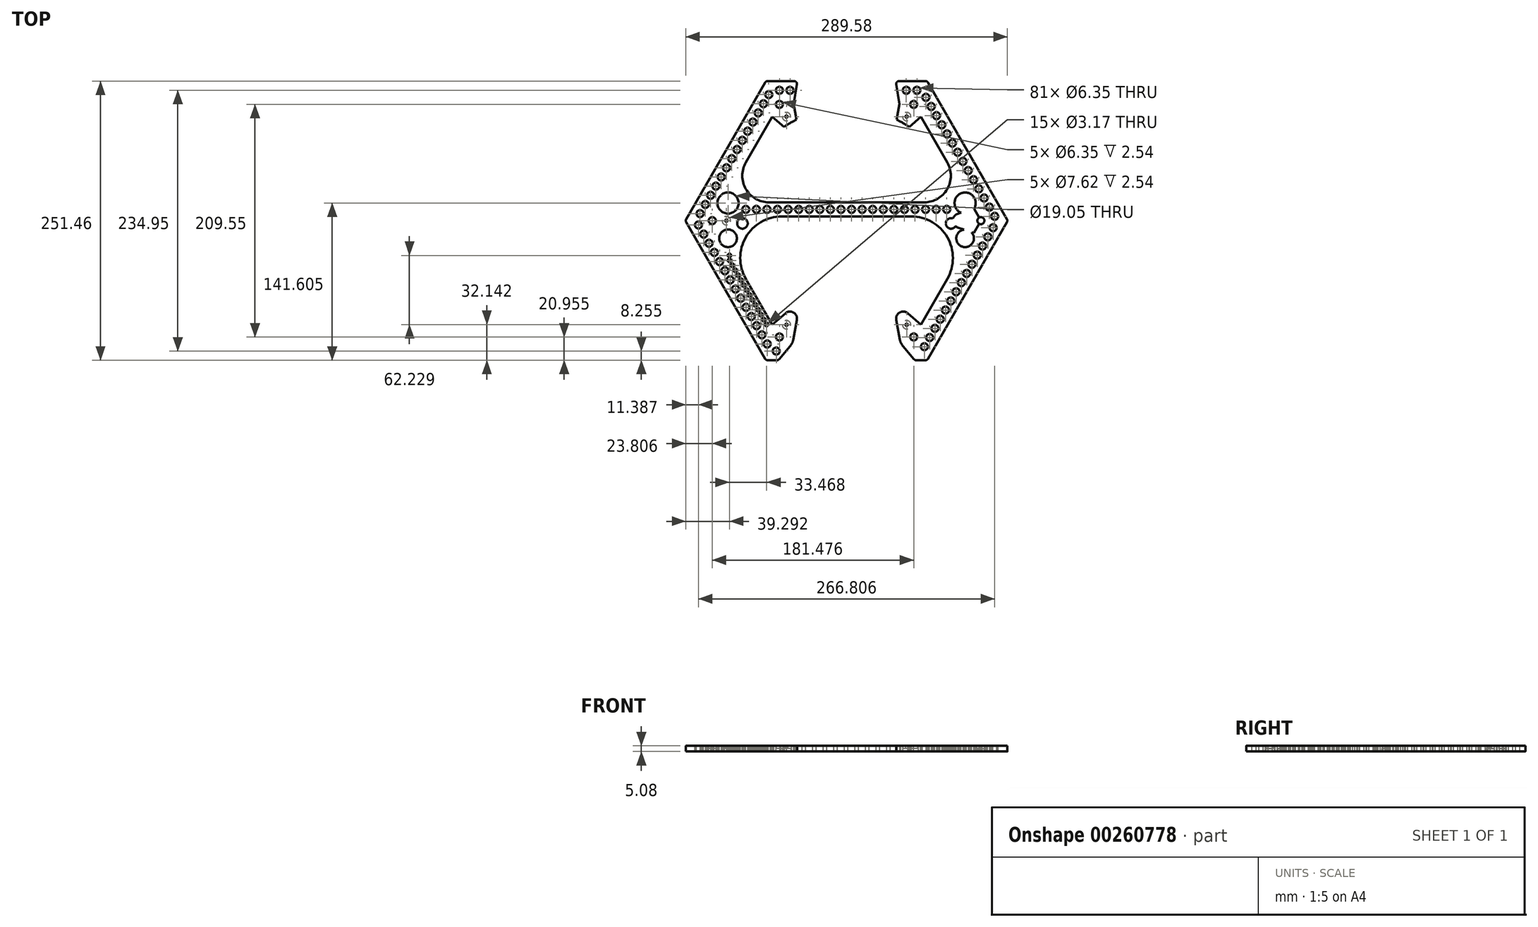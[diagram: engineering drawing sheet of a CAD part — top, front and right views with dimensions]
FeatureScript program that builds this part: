
annotation { "Feature Type Name" : "Feature", "Feature Type Description" : "" }
export const myFeature = defineFeature(function(context is Context, id is Id, definition is map)
    precondition{}
    {
        {
            var Q0;
            Q0=qCreatedBy(makeId("Top.planeOp"),FACE);
            var sketch = newSketch(context, id + "F0", { "sketchPlane" : qUnion([Q0])});
            skCircle(sketch, "E0.cCircle", {"center": v(0, 0) * mm, "radius": 125.73 * mm, "construction": true});
            skLineSegment(sketch, "E0.0", {"start": v(-72.6, 125.73) * mm, "end": v(72.6, 125.73) * mm, "construction": true});
            skLineSegment(sketch, "E0.1", {"start": v(72.6, 125.73) * mm, "end": v(145.18, 0) * mm, "construction": true});
            skLineSegment(sketch, "E0.2", {"start": v(145.18, 0) * mm, "end": v(72.6, -125.73) * mm, "construction": true});
            skLineSegment(sketch, "E0.3", {"start": v(72.6, -125.73) * mm, "end": v(-72.6, -125.73) * mm, "construction": true});
            skLineSegment(sketch, "E0.4", {"start": v(-72.6, -125.73) * mm, "end": v(-145.18, 0) * mm, "construction": true});
            skLineSegment(sketch, "E0.5", {"start": v(-145.18, 0) * mm, "end": v(-72.6, 125.73) * mm, "construction": true});
            skPoint(sketch, "E0.0.midPoint", {"position": v(0, 125.73) * mm});
            skLineSegment(sketch, "E1.bottom", {"start": v(-23.4, 2.97) * mm, "end": v(23.4, 2.97) * mm, "construction": true});
            skLineSegment(sketch, "E1.top", {"start": v(-23.4, -102.03) * mm, "end": v(23.4, -102.03) * mm, "construction": true});
            skLineSegment(sketch, "E1.left", {"start": v(-61.5, -35.13) * mm, "end": v(-61.5, -63.93) * mm, "construction": true});
            skLineSegment(sketch, "E1.right", {"start": v(61.5, -35.13) * mm, "end": v(61.5, -63.93) * mm, "construction": true});
            skPoint(sketch, "E2", {"position": v(0, -49.53) * mm});
            skPoint(sketch, "E2.positionSnap0", {"position": v(61.5, -49.53) * mm});
            skPoint(sketch, "E2.positionSnap1", {"position": v(0, 2.97) * mm});
            skPoint(sketch, "E3.visualSharp", {"position": v(-61.5, 2.97) * mm});
            skArc(sketch, "E3.filletArc", {"start": v(-23.4, 2.97) * mm, "mid": v(-50.34, -8.19) * mm, "end": v(-61.5, -35.13) * mm, "construction": true});
            skPoint(sketch, "E4.visualSharp", {"position": v(-61.5, -102.03) * mm});
            skArc(sketch, "E4.filletArc", {"start": v(-61.5, -63.93) * mm, "mid": v(-50.34, -90.87) * mm, "end": v(-23.4, -102.03) * mm, "construction": true});
            skPoint(sketch, "E5.visualSharp", {"position": v(61.5, -102.03) * mm});
            skArc(sketch, "E5.filletArc", {"start": v(23.4, -102.03) * mm, "mid": v(50.34, -90.87) * mm, "end": v(61.5, -63.93) * mm, "construction": true});
            skPoint(sketch, "E6.visualSharp", {"position": v(61.5, 2.97) * mm});
            skArc(sketch, "E6.filletArc", {"start": v(61.5, -35.13) * mm, "mid": v(50.34, -8.19) * mm, "end": v(23.4, 2.97) * mm, "construction": true});
            skLineSegment(sketch, "E7.bottom", {"start": v(-44.25, 106.48) * mm, "end": v(44.25, 106.48) * mm, "construction": true});
            skLineSegment(sketch, "E7.top", {"start": v(-44.25, 17.98) * mm, "end": v(44.25, 17.98) * mm, "construction": true});
            skLineSegment(sketch, "E7.left", {"start": v(-44.25, 106.48) * mm, "end": v(-44.25, 17.98) * mm, "construction": true});
            skLineSegment(sketch, "E7.right", {"start": v(44.25, 106.48) * mm, "end": v(44.25, 17.98) * mm, "construction": true});
            skPoint(sketch, "E8", {"position": v(0, 106.48) * mm});
            skPoint(sketch, "E9", {"position": v(0, 62.23) * mm});
            skPoint(sketch, "E9.positionSnap0", {"position": v(-44.25, 62.23) * mm});
            skSolve(sketch);
        }
        {
            var Q0;
            Q0=qCreatedBy(makeId("Top.planeOp"),FACE);
            var sketch = newSketch(context, id + "F1", { "sketchPlane" : qUnion([Q0])});
            skLineSegment(sketch, "E10", {"start": v(-73.32, 124.46) * mm, "end": v(-144.45, 1.27) * mm});
            skLineSegment(sketch, "E11", {"start": v(-144.45, -1.27) * mm, "end": v(-73.32, -124.46) * mm});
            skLineSegment(sketch, "E12", {"start": v(-71.12, -125.73) * mm, "end": v(-62.68, -125.73) * mm});
            skLineSegment(sketch, "E13", {"start": v(-71.12, 125.73) * mm, "end": v(-47.23, 125.73) * mm});
            skLineSegment(sketch, "E14", {"start": v(47.23, 125.73) * mm, "end": v(71.12, 125.73) * mm});
            skLineSegment(sketch, "E15", {"start": v(73.32, 124.46) * mm, "end": v(144.45, 1.27) * mm});
            skLineSegment(sketch, "E16", {"start": v(144.45, -1.27) * mm, "end": v(73.32, -124.46) * mm});
            skLineSegment(sketch, "E17", {"start": v(71.12, -125.73) * mm, "end": v(62.68, -125.73) * mm});
            skCircle(sketch, "E18.cCircle", {"center": v(0, 0) * mm, "radius": 104.78 * mm, "construction": true});
            skLineSegment(sketch, "E18.0", {"start": v(-60.5, 104.78) * mm, "end": v(60.5, 104.78) * mm, "construction": true});
            skLineSegment(sketch, "E18.1", {"start": v(60.5, 104.78) * mm, "end": v(120.98, 0) * mm});
            skLineSegment(sketch, "E18.2", {"start": v(120.98, 0) * mm, "end": v(60.5, -104.78) * mm});
            skLineSegment(sketch, "E18.3", {"start": v(60.5, -104.77) * mm, "end": v(-60.5, -104.78) * mm, "construction": true});
            skLineSegment(sketch, "E18.4", {"start": v(-60.5, -104.78) * mm, "end": v(-120.98, 0) * mm});
            skLineSegment(sketch, "E18.5", {"start": v(-120.98, 0) * mm, "end": v(-60.5, 104.78) * mm});
            skPoint(sketch, "E18.0.midPoint", {"position": v(0, 104.78) * mm});
            skCircle(sketch, "E19", {"center": v(-60.5, 104.78) * mm, "radius": 3.18 * mm});
            skCircle(sketch, "E20", {"center": v(60.5, 104.78) * mm, "radius": 3.18 * mm});
            skCircle(sketch, "E21", {"center": v(-120.98, 0) * mm, "radius": 3.18 * mm});
            skCircle(sketch, "E22", {"center": v(120.98, 0) * mm, "radius": 3.17 * mm});
            skCircle(sketch, "E23", {"center": v(60.5, -104.78) * mm, "radius": 3.18 * mm});
            skCircle(sketch, "E24", {"center": v(-60.5, -104.78) * mm, "radius": 3.17 * mm});
            skCircle(sketch, "E25", {"center": v(-60.5, -104.78) * mm, "radius": 12.7 * mm, "construction": true});
            skCircle(sketch, "E26", {"center": v(60.5, -104.78) * mm, "radius": 12.7 * mm, "construction": true});
            skLineSegment(sketch, "E27", {"start": v(-60.74, -124.82) * mm, "end": v(-50.76, -112.94) * mm});
            skPoint(sketch, "E28.visualSharp", {"position": v(-72.6, -125.73) * mm});
            skArc(sketch, "E28.filletArc", {"start": v(-73.32, -124.46) * mm, "mid": v(-72.4, -125.39) * mm, "end": v(-71.12, -125.73) * mm});
            skPoint(sketch, "E29.visualSharp", {"position": v(-61.5, -125.73) * mm});
            skArc(sketch, "E29.filletArc", {"start": v(-62.68, -125.73) * mm, "mid": v(-61.61, -125.5) * mm, "end": v(-60.74, -124.82) * mm});
            skCircle(sketch, "E30", {"center": v(-120.98, 0) * mm, "radius": 12.7 * mm, "construction": true});
            skCircle(sketch, "E31", {"center": v(120.98, 0) * mm, "radius": 12.7 * mm, "construction": true});
            skCircle(sketch, "E32", {"center": v(60.5, 104.78) * mm, "radius": 12.7 * mm, "construction": true});
            skCircle(sketch, "E33", {"center": v(-60.5, 104.78) * mm, "radius": 12.7 * mm, "construction": true});
            skLineSegment(sketch, "E34", {"start": v(-44.72, 122.79) * mm, "end": v(-47.95, 102.75) * mm});
            skLineSegment(sketch, "E35", {"start": v(-51.48, 95.8) * mm, "end": v(-51.07, 96.26) * mm});
            skArc(sketch, "E36", {"start": v(-51.07, 96.26) * mm, "mid": v(-49.04, 99.28) * mm, "end": v(-47.95, 102.75) * mm});
            skArc(sketch, "E37", {"start": v(-50.76, -112.94) * mm, "mid": v(-47.8, -104.54) * mm, "end": v(-51.07, -96.26) * mm});
            skLineSegment(sketch, "E38", {"start": v(60.74, -124.82) * mm, "end": v(50.76, -112.94) * mm});
            skLineSegment(sketch, "E39", {"start": v(44.72, 122.79) * mm, "end": v(47.95, 102.75) * mm});
            skLineSegment(sketch, "E40", {"start": v(51.48, 95.8) * mm, "end": v(51.07, 96.26) * mm});
            skArc(sketch, "E41", {"start": v(47.95, 102.75) * mm, "mid": v(49.04, 99.28) * mm, "end": v(51.07, 96.26) * mm});
            skArc(sketch, "E42", {"start": v(51.07, -96.26) * mm, "mid": v(47.8, -104.54) * mm, "end": v(50.76, -112.94) * mm});
            skPoint(sketch, "E43.visualSharp", {"position": v(-90.74, -52.39) * mm});
            skPoint(sketch, "E44.visualSharp", {"position": v(90.74, -52.39) * mm});
            skPoint(sketch, "E45.visualSharp", {"position": v(-90.74, 52.39) * mm});
            skPoint(sketch, "E46.visualSharp", {"position": v(90.74, 52.39) * mm});
            skPoint(sketch, "E47.visualSharp", {"position": v(-44.25, 125.73) * mm});
            skArc(sketch, "E47.filletArc", {"start": v(-44.72, 122.79) * mm, "mid": v(-45.3, 124.84) * mm, "end": v(-47.23, 125.73) * mm});
            skPoint(sketch, "E48.visualSharp", {"position": v(-145.18, 0) * mm});
            skArc(sketch, "E48.filletArc", {"start": v(-144.45, 1.27) * mm, "mid": v(-144.79, 0) * mm, "end": v(-144.45, -1.27) * mm});
            skPoint(sketch, "E49.visualSharp", {"position": v(-72.6, 125.73) * mm});
            skArc(sketch, "E49.filletArc", {"start": v(-71.12, 125.73) * mm, "mid": v(-72.4, 125.39) * mm, "end": v(-73.32, 124.46) * mm});
            skPoint(sketch, "E50.visualSharp", {"position": v(44.25, 125.73) * mm});
            skArc(sketch, "E50.filletArc", {"start": v(47.23, 125.73) * mm, "mid": v(45.3, 124.84) * mm, "end": v(44.72, 122.79) * mm});
            skPoint(sketch, "E51.visualSharp", {"position": v(72.6, 125.73) * mm});
            skArc(sketch, "E51.filletArc", {"start": v(73.32, 124.46) * mm, "mid": v(72.4, 125.39) * mm, "end": v(71.12, 125.73) * mm});
            skPoint(sketch, "E52.visualSharp", {"position": v(145.18, 0) * mm});
            skArc(sketch, "E52.filletArc", {"start": v(144.45, -1.27) * mm, "mid": v(144.79, 0) * mm, "end": v(144.45, 1.27) * mm});
            skPoint(sketch, "E53.visualSharp", {"position": v(72.6, -125.73) * mm});
            skArc(sketch, "E53.filletArc", {"start": v(71.12, -125.73) * mm, "mid": v(72.4, -125.39) * mm, "end": v(73.32, -124.46) * mm});
            skPoint(sketch, "E54.visualSharp", {"position": v(61.5, -125.73) * mm});
            skArc(sketch, "E54.filletArc", {"start": v(60.74, -124.82) * mm, "mid": v(61.61, -125.5) * mm, "end": v(62.68, -125.73) * mm});
            skLineSegment(sketch, "E55", {"start": v(-48, 107.1) * mm, "end": v(-44.72, 89.44) * mm});
            skLineSegment(sketch, "E56", {"start": v(-55.1, 83.45) * mm, "end": v(-68.74, 95.12) * mm});
            skLineSegment(sketch, "E57", {"start": v(-41.44, 71.78) * mm, "end": v(-60.5, 104.78) * mm, "construction": true});
            skArc(sketch, "E58.filletArc", {"start": v(-55.1, 83.45) * mm, "mid": v(-47.8, 82.78) * mm, "end": v(-44.72, 89.44) * mm});
            skPoint(sketch, "E59.startSnap0", {"position": v(46.34, 112.77) * mm});
            skLineSegment(sketch, "E60", {"start": v(48, 107.1) * mm, "end": v(44.72, 89.44) * mm});
            skLineSegment(sketch, "E61", {"start": v(55.1, 83.45) * mm, "end": v(68.74, 95.12) * mm});
            skLineSegment(sketch, "E62", {"start": v(41.44, 71.78) * mm, "end": v(60.5, 104.78) * mm, "construction": true});
            skArc(sketch, "E63.filletArc", {"start": v(44.72, 89.44) * mm, "mid": v(47.8, 82.78) * mm, "end": v(55.1, 83.45) * mm});
            skLineSegment(sketch, "E64.MirrorCS", {"start": v(-41.44, -71.78) * mm, "end": v(-60.5, -104.78) * mm, "construction": true});
            skLineSegment(sketch, "E65.MirrorCS", {"start": v(41.44, -71.78) * mm, "end": v(60.5, -104.78) * mm, "construction": true});
            skLineSegment(sketch, "E66.MirrorCS", {"start": v(55.1, -83.45) * mm, "end": v(68.74, -95.12) * mm});
            skArc(sketch, "E67.MirrorCS", {"start": v(44.72, -89.44) * mm, "mid": v(47.8, -82.78) * mm, "end": v(55.1, -83.45) * mm});
            skLineSegment(sketch, "E68.MirrorCS", {"start": v(48, -107.1) * mm, "end": v(44.72, -89.44) * mm});
            skArc(sketch, "E69.MirrorCS", {"start": v(-55.1, -83.45) * mm, "mid": v(-47.8, -82.78) * mm, "end": v(-44.72, -89.44) * mm});
            skLineSegment(sketch, "E70.MirrorCS", {"start": v(-48, -107.1) * mm, "end": v(-44.72, -89.44) * mm});
            skLineSegment(sketch, "E71.MirrorCS", {"start": v(-55.1, -83.45) * mm, "end": v(-68.74, -95.12) * mm});
            skLineSegment(sketch, "E72", {"start": v(-116.75, 11.97) * mm, "end": v(-99.82, 5.99) * mm});
            skLineSegment(sketch, "E73", {"start": v(-99.82, -5.99) * mm, "end": v(-116.75, -11.97) * mm});
            skLineSegment(sketch, "E74", {"start": v(-82.88, 0) * mm, "end": v(-120.98, 0) * mm, "construction": true});
            skPoint(sketch, "E75.visualSharp", {"position": v(-82.88, 0) * mm});
            skArc(sketch, "E75.filletArc", {"start": v(-99.82, -5.99) * mm, "mid": v(-95.58, 0) * mm, "end": v(-99.82, 5.99) * mm});
            skLineSegment(sketch, "E76.MirrorCS", {"start": v(116.75, 11.97) * mm, "end": v(99.82, 5.99) * mm});
            skArc(sketch, "E77.MirrorCS", {"start": v(99.82, -5.99) * mm, "mid": v(95.58, 0) * mm, "end": v(99.82, 5.99) * mm});
            skLineSegment(sketch, "E78.MirrorCS", {"start": v(82.88, 0) * mm, "end": v(120.98, 0) * mm, "construction": true});
            skLineSegment(sketch, "E79.MirrorCS", {"start": v(99.82, -5.99) * mm, "end": v(116.75, -11.97) * mm});
            skCircle(sketch, "E80", {"center": v(-108.28, 0) * mm, "radius": 1.08 * mm});
            skCircle(sketch, "E81", {"center": v(-54.14, -93.78) * mm, "radius": 1.08 * mm});
            skCircle(sketch, "E82", {"center": v(54.14, -93.78) * mm, "radius": 1.08 * mm});
            skCircle(sketch, "E83", {"center": v(108.28, 0) * mm, "radius": 1.08 * mm});
            skCircle(sketch, "E84", {"center": v(54.14, 93.78) * mm, "radius": 1.08 * mm});
            skCircle(sketch, "E85", {"center": v(-54.14, 93.78) * mm, "radius": 1.08 * mm});
            skArc(sketch, "E86", {"start": v(-58.26, 3.86) * mm, "mid": v(-90.74, -14.9) * mm, "end": v(-90.74, -52.39) * mm});
            skArc(sketch, "E87", {"start": v(-90.74, 52.39) * mm, "mid": v(-90.74, 28.47) * mm, "end": v(-70.02, 16.5) * mm});
            skLineSegment(sketch, "E88", {"start": v(-70.02, 16.5) * mm, "end": v(70.02, 16.5) * mm});
            skLineSegment(sketch, "E89", {"start": v(-58.26, 3.86) * mm, "end": v(58.26, 3.86) * mm});
            skPoint(sketch, "E90", {"position": v(0, 3.86) * mm});
            skPoint(sketch, "E91", {"position": v(0, 16.5) * mm});
            skArc(sketch, "E92", {"start": v(90.74, -52.39) * mm, "mid": v(90.74, -14.9) * mm, "end": v(58.26, 3.86) * mm});
            skArc(sketch, "E93", {"start": v(70.02, 16.5) * mm, "mid": v(90.74, 28.47) * mm, "end": v(90.74, 52.39) * mm});
            skSolve(sketch);
        }
        {
            var Q0;
            {var subQ2=sQuery(id+"F1.wireOp",EDGE,"E35");Q0=makeQuery(id+"F1.imprint","IMPRINT",FACE,{"disambiguationData":[TD([[makeQuery(id+"F1.imprint","IMPRINT",EDGE,{"derivedFrom":subQ2}),-1.0]])]});}
            var Q1;
            {var subQ4=sQuery(id+"F1.wireOp",EDGE,"E69.MirrorCS");Q1=makeQuery(id+"F1.imprint","IMPRINT",FACE,{"disambiguationData":[TD([[makeQuery(id+"F1.imprint","IMPRINT",EDGE,{"derivedFrom":subQ4}),-1.0]])]});}
            var Q2;
            {var subQ6=sQuery(id+"F1.wireOp",EDGE,"E40");Q2=makeQuery(id+"F1.imprint","IMPRINT",FACE,{"disambiguationData":[TD([[makeQuery(id+"F1.imprint","IMPRINT",EDGE,{"derivedFrom":subQ6}),1.0]])]});}
            var Q3;
            {var subQ6=sQuery(id+"F1.wireOp",EDGE,"E67.MirrorCS");Q3=makeQuery(id+"F1.imprint","IMPRINT",FACE,{"disambiguationData":[TD([[makeQuery(id+"F1.imprint","IMPRINT",EDGE,{"derivedFrom":subQ6}),-1.0]])]});}
            var Q4;
            Q4=makeQuery(id+"F1.imprint","IMPRINT",FACE,{"disambiguationData":[TD([[makeQuery(id+"F1.imprint","IMPRINT",EDGE,{"derivedFrom":sQuery(id+"F1.wireOp",EDGE,"E10")}),1.0]])]});
            var Q5;
            Q5=makeQuery(id+"F1.imprint","IMPRINT",FACE,{"disambiguationData":[TD([[makeQuery(id+"F1.imprint","IMPRINT",EDGE,{"derivedFrom":sQuery(id+"F1.wireOp",EDGE,"E14")}),-1.0]])]});
            var Q6;
            {var subQ0=sQuery(id+"F1.wireOp",EDGE,"E75.filletArc");Q6=makeQuery(id+"F1.imprint","IMPRINT",FACE,{"disambiguationData":[TD([[makeQuery(id+"F1.imprint","IMPRINT",EDGE,{"derivedFrom":subQ0}),1.0]])]});}
            var Q7;
            {var subQ0=sQuery(id+"F1.wireOp",EDGE,"E77.MirrorCS");Q7=makeQuery(id+"F1.imprint","IMPRINT",FACE,{"disambiguationData":[TD([[makeQuery(id+"F1.imprint","IMPRINT",EDGE,{"derivedFrom":subQ0}),-1.0]])]});}
            var Q8;
            {var subQ11=sQuery(id+"F1.wireOp",EDGE,"E75.filletArc");Q8=makeQuery(id+"F1.imprint","IMPRINT",FACE,{"disambiguationData":[TD([[makeQuery(id+"F1.imprint","IMPRINT",EDGE,{"derivedFrom":subQ11}),-1.0]])]});}
            extrude(context, id + "F2", {"entities" : qUnion([Q0, Q1, Q2, Q3, Q4, Q5, Q6, Q7, Q8]), "depth" : 5.08 * mm});
        }
        {
            var Q0;
            Q0=makeQuery(id+"F1.imprint","IMPRINT",FACE,{"disambiguationData":[TD([[makeQuery(id+"F1.imprint","IMPRINT",EDGE,{"derivedFrom":sQuery(id+"F1.wireOp",EDGE,"E19")}),1.0]])]});
            var Q1;
            Q1=makeQuery(id+"F1.imprint","IMPRINT",FACE,{"disambiguationData":[TD([[makeQuery(id+"F1.imprint","IMPRINT",EDGE,{"derivedFrom":sQuery(id+"F1.wireOp",EDGE,"E20")}),1.0]])]});
            var Q2;
            Q2=makeQuery(id+"F1.imprint","IMPRINT",FACE,{"disambiguationData":[TD([[makeQuery(id+"F1.imprint","IMPRINT",EDGE,{"derivedFrom":sQuery(id+"F1.wireOp",EDGE,"E21")}),1.0]])]});
            var Q3;
            Q3=makeQuery(id+"F1.imprint","IMPRINT",FACE,{"disambiguationData":[TD([[makeQuery(id+"F1.imprint","IMPRINT",EDGE,{"derivedFrom":sQuery(id+"F1.wireOp",EDGE,"E22")}),1.0]])]});
            var Q4;
            Q4=makeQuery(id+"F1.imprint","IMPRINT",FACE,{"disambiguationData":[TD([[makeQuery(id+"F1.imprint","IMPRINT",EDGE,{"derivedFrom":sQuery(id+"F1.wireOp",EDGE,"E23")}),1.0]])]});
            var Q5;
            Q5=makeQuery(id+"F1.imprint","IMPRINT",FACE,{"disambiguationData":[TD([[makeQuery(id+"F1.imprint","IMPRINT",EDGE,{"derivedFrom":sQuery(id+"F1.wireOp",EDGE,"E24")}),1.0]])]});
            extrude(context, id + "F3", {"entities" : qUnion([Q0, Q1, Q2, Q3, Q4, Q5]), "operationType" : NewBodyOperationType.ADD, "depth" : 2.54 * mm});
        }
        {
            var Q0;
            Q0=makeQuery(id+"F1.imprint","IMPRINT",FACE,{"disambiguationData":[TD([[makeQuery(id+"F1.imprint","IMPRINT",EDGE,{"derivedFrom":sQuery(id+"F1.wireOp",EDGE,"E10")}),1.0]])]});
            var sketch = newSketch(context, id + "F4", { "sketchPlane" : qUnion([Q0])});
            skCircle(sketch, "E94", {"center": v(54.14, 93.78) * mm, "radius": 3.81 * mm});
            skCircle(sketch, "E95", {"center": v(-54.14, 93.78) * mm, "radius": 3.81 * mm});
            skCircle(sketch, "E96", {"center": v(-108.28, 0) * mm, "radius": 3.81 * mm});
            skCircle(sketch, "E97", {"center": v(108.28, 0) * mm, "radius": 3.81 * mm});
            skCircle(sketch, "E98", {"center": v(54.14, -93.78) * mm, "radius": 3.81 * mm});
            skCircle(sketch, "E99", {"center": v(-54.14, -93.78) * mm, "radius": 3.81 * mm});
            skSolve(sketch);
        }
        {
            var Q0;
            Q0 = qSketchRegion(id + "F4", true);
            extrude(context, id + "F5", {"entities" : qUnion([Q0]), "operationType" : NewBodyOperationType.REMOVE, "depth" : 2.54 * mm});
        }
        {
            var Q0;
            Q0=makeQuery(id+"F2.opExtrude","CAP_FACE",FACE,{"disambiguationData":[OSD([sQuery(id+"F1.wireOp",EDGE,"E10"),sQuery(id+"F1.wireOp",EDGE,"E11"),sQuery(id+"F1.wireOp",EDGE,"E12"),sQuery(id+"F1.wireOp",EDGE,"E13"),sQuery(id+"F1.wireOp",EDGE,"E14"),sQuery(id+"F1.wireOp",EDGE,"E15"),sQuery(id+"F1.wireOp",EDGE,"E16"),sQuery(id+"F1.wireOp",EDGE,"E17"),sQuery(id+"F1.wireOp",EDGE,"E18.1"),sQuery(id+"F1.wireOp",EDGE,"E18.2"),sQuery(id+"F1.wireOp",EDGE,"E18.4"),sQuery(id+"F1.wireOp",EDGE,"E18.5"),sQuery(id+"F1.wireOp",EDGE,"E19"),sQuery(id+"F1.wireOp",EDGE,"E20"),sQuery(id+"F1.wireOp",EDGE,"E21"),sQuery(id+"F1.wireOp",EDGE,"E22"),sQuery(id+"F1.wireOp",EDGE,"E23"),sQuery(id+"F1.wireOp",EDGE,"E24"),sQuery(id+"F1.wireOp",EDGE,"E27"),sQuery(id+"F1.wireOp",EDGE,"E28.filletArc"),sQuery(id+"F1.wireOp",EDGE,"E29.filletArc"),sQuery(id+"F1.wireOp",EDGE,"E34"),sQuery(id+"F1.wireOp",EDGE,"E37"),sQuery(id+"F1.wireOp",EDGE,"E38"),sQuery(id+"F1.wireOp",EDGE,"E39"),sQuery(id+"F1.wireOp",EDGE,"E42"),sQuery(id+"F1.wireOp",EDGE,"E47.filletArc"),sQuery(id+"F1.wireOp",EDGE,"E48.filletArc"),sQuery(id+"F1.wireOp",EDGE,"E49.filletArc"),sQuery(id+"F1.wireOp",EDGE,"E50.filletArc"),sQuery(id+"F1.wireOp",EDGE,"E51.filletArc"),sQuery(id+"F1.wireOp",EDGE,"E52.filletArc"),sQuery(id+"F1.wireOp",EDGE,"E53.filletArc"),sQuery(id+"F1.wireOp",EDGE,"E54.filletArc"),sQuery(id+"F1.wireOp",EDGE,"E55"),sQuery(id+"F1.wireOp",EDGE,"E56"),sQuery(id+"F1.wireOp",EDGE,"E58.filletArc"),sQuery(id+"F1.wireOp",EDGE,"E60"),sQuery(id+"F1.wireOp",EDGE,"E61"),sQuery(id+"F1.wireOp",EDGE,"E63.filletArc"),sQuery(id+"F1.wireOp",EDGE,"E66.MirrorCS"),sQuery(id+"F1.wireOp",EDGE,"E67.MirrorCS"),sQuery(id+"F1.wireOp",EDGE,"E68.MirrorCS"),sQuery(id+"F1.wireOp",EDGE,"E69.MirrorCS"),sQuery(id+"F1.wireOp",EDGE,"E70.MirrorCS"),sQuery(id+"F1.wireOp",EDGE,"E71.MirrorCS"),sQuery(id+"F1.wireOp",EDGE,"E80"),sQuery(id+"F1.wireOp",EDGE,"E81"),sQuery(id+"F1.wireOp",EDGE,"E82"),sQuery(id+"F1.wireOp",EDGE,"E83"),sQuery(id+"F1.wireOp",EDGE,"E84"),sQuery(id+"F1.wireOp",EDGE,"E85"),sQuery(id+"F1.wireOp",EDGE,"E86"),sQuery(id+"F1.wireOp",EDGE,"E87"),sQuery(id+"F1.wireOp",EDGE,"E88"),sQuery(id+"F1.wireOp",EDGE,"E89"),sQuery(id+"F1.wireOp",EDGE,"E92"),sQuery(id+"F1.wireOp",EDGE,"E93")])],"isStart":false});
            var sketch = newSketch(context, id + "F6", { "sketchPlane" : qUnion([Q0])});
            skCircle(sketch, "E100.cCircle", {"center": v(0, 0) * mm, "radius": 117.48 * mm, "construction": true});
            skLineSegment(sketch, "E100.0", {"start": v(-67.82, 117.48) * mm, "end": v(67.82, 117.48) * mm, "construction": true});
            skLineSegment(sketch, "E100.1", {"start": v(67.82, 117.48) * mm, "end": v(135.65, 0) * mm, "construction": true});
            skLineSegment(sketch, "E100.2", {"start": v(135.65, 0) * mm, "end": v(67.82, -117.47) * mm, "construction": true});
            skLineSegment(sketch, "E100.3", {"start": v(67.82, -117.47) * mm, "end": v(-67.82, -117.48) * mm, "construction": true});
            skLineSegment(sketch, "E100.4", {"start": v(-67.82, -117.48) * mm, "end": v(-135.65, 0) * mm, "construction": true});
            skLineSegment(sketch, "E100.5", {"start": v(-135.65, 0) * mm, "end": v(-67.82, 117.48) * mm, "construction": true});
            skPoint(sketch, "E100.0.midPoint", {"position": v(0, 117.48) * mm});
            skCircle(sketch, "E101", {"center": v(-60.5, 117.48) * mm, "radius": 3.18 * mm});
            skPoint(sketch, "E102", {"position": v(-60.5, 104.78) * mm});
            skCircle(sketch, "E103.1.0.0", {"center": v(-50.97, 117.48) * mm, "radius": 3.18 * mm});
            skCircle(sketch, "E103.2.0.0", {"center": v(-41.44, 117.48) * mm, "radius": 3.18 * mm});
            skCircle(sketch, "E103.3.0.0", {"center": v(-31.92, 117.48) * mm, "radius": 3.18 * mm});
            skCircle(sketch, "E103.4.0.0", {"center": v(-22.4, 117.48) * mm, "radius": 3.18 * mm});
            skCircle(sketch, "E103.5.0.0", {"center": v(-12.87, 117.48) * mm, "radius": 3.18 * mm});
            skCircle(sketch, "E103.6.0.0", {"center": v(-3.34, 117.48) * mm, "radius": 3.18 * mm});
            skCircle(sketch, "E103.7.0.0", {"center": v(6.18, 117.48) * mm, "radius": 3.18 * mm});
            skCircle(sketch, "E103.8.0.0", {"center": v(15.7, 117.48) * mm, "radius": 3.18 * mm});
            skCircle(sketch, "E103.9.0.0", {"center": v(25.23, 117.48) * mm, "radius": 3.18 * mm});
            skCircle(sketch, "E103.10.0.0", {"center": v(34.76, 117.48) * mm, "radius": 3.18 * mm});
            skCircle(sketch, "E103.12.0.0", {"center": v(53.8, 117.48) * mm, "radius": 3.18 * mm});
            skCircle(sketch, "E103.13.0.0", {"center": v(63.33, 117.48) * mm, "radius": 3.18 * mm});
            skLineSegment(sketch, "E103.direction1", {"start": v(-60.5, 117.48) * mm, "end": v(-50.97, 117.48) * mm, "construction": true});
            skCircle(sketch, "E104.1.0", {"center": v(-117.7, 31.1) * mm, "radius": 3.18 * mm});
            skCircle(sketch, "E104.1.1", {"center": v(-122.46, 22.85) * mm, "radius": 3.18 * mm});
            skCircle(sketch, "E104.1.2", {"center": v(-127.22, 14.6) * mm, "radius": 3.18 * mm});
            skCircle(sketch, "E104.1.3", {"center": v(-131.98, 6.35) * mm, "radius": 3.18 * mm});
            skCircle(sketch, "E104.1.4", {"center": v(-112.93, 39.35) * mm, "radius": 3.18 * mm});
            skCircle(sketch, "E104.1.5", {"center": v(-108.17, 47.6) * mm, "radius": 3.18 * mm});
            skCircle(sketch, "E104.1.6", {"center": v(-103.4, 55.84) * mm, "radius": 3.18 * mm});
            skCircle(sketch, "E104.1.7", {"center": v(-98.64, 64.1) * mm, "radius": 3.18 * mm});
            skCircle(sketch, "E104.1.8", {"center": v(-93.88, 72.34) * mm, "radius": 3.18 * mm});
            skCircle(sketch, "E104.1.9", {"center": v(-89.12, 80.6) * mm, "radius": 3.18 * mm});
            skCircle(sketch, "E104.1.10", {"center": v(-84.36, 88.84) * mm, "radius": 3.18 * mm});
            skCircle(sketch, "E104.1.11", {"center": v(-79.6, 97.09) * mm, "radius": 3.18 * mm});
            skCircle(sketch, "E104.1.12", {"center": v(-74.83, 105.34) * mm, "radius": 3.18 * mm});
            skCircle(sketch, "E104.1.13", {"center": v(-70.07, 113.59) * mm, "radius": 3.18 * mm});
            skCircle(sketch, "E104.2.0", {"center": v(-85.78, -86.38) * mm, "radius": 3.18 * mm});
            skCircle(sketch, "E104.2.1", {"center": v(-81.02, -94.63) * mm, "radius": 3.18 * mm});
            skCircle(sketch, "E104.2.2", {"center": v(-76.25, -102.88) * mm, "radius": 3.18 * mm});
            skCircle(sketch, "E104.2.3", {"center": v(-71.5, -111.12) * mm, "radius": 3.18 * mm});
            skCircle(sketch, "E104.2.4", {"center": v(-90.54, -78.13) * mm, "radius": 3.18 * mm});
            skCircle(sketch, "E104.2.5", {"center": v(-95.3, -69.88) * mm, "radius": 3.18 * mm});
            skCircle(sketch, "E104.2.6", {"center": v(-100.07, -61.63) * mm, "radius": 3.18 * mm});
            skCircle(sketch, "E104.2.7", {"center": v(-104.83, -53.38) * mm, "radius": 3.18 * mm});
            skCircle(sketch, "E104.2.8", {"center": v(-109.6, -45.13) * mm, "radius": 3.18 * mm});
            skCircle(sketch, "E104.2.9", {"center": v(-114.35, -36.88) * mm, "radius": 3.18 * mm});
            skCircle(sketch, "E104.2.10", {"center": v(-119.12, -28.64) * mm, "radius": 3.18 * mm});
            skCircle(sketch, "E104.2.11", {"center": v(-123.88, -20.39) * mm, "radius": 3.18 * mm});
            skCircle(sketch, "E104.2.12", {"center": v(-128.64, -12.14) * mm, "radius": 3.18 * mm});
            skCircle(sketch, "E104.2.13", {"center": v(-133.4, -3.89) * mm, "radius": 3.18 * mm});
            skCircle(sketch, "E104.3.0", {"center": v(31.92, -117.48) * mm, "radius": 3.18 * mm});
            skCircle(sketch, "E104.3.1", {"center": v(41.44, -117.48) * mm, "radius": 3.18 * mm});
            skCircle(sketch, "E104.3.4", {"center": v(22.4, -117.48) * mm, "radius": 3.18 * mm});
            skCircle(sketch, "E104.3.5", {"center": v(12.87, -117.48) * mm, "radius": 3.18 * mm});
            skCircle(sketch, "E104.3.6", {"center": v(3.34, -117.48) * mm, "radius": 3.18 * mm});
            skCircle(sketch, "E104.3.7", {"center": v(-6.18, -117.48) * mm, "radius": 3.18 * mm});
            skCircle(sketch, "E104.3.8", {"center": v(-15.7, -117.48) * mm, "radius": 3.18 * mm});
            skCircle(sketch, "E104.3.9", {"center": v(-25.23, -117.48) * mm, "radius": 3.18 * mm});
            skCircle(sketch, "E104.3.10", {"center": v(-34.76, -117.48) * mm, "radius": 3.18 * mm});
            skCircle(sketch, "E104.3.11", {"center": v(-44.28, -117.48) * mm, "radius": 3.18 * mm});
            skCircle(sketch, "E104.3.13", {"center": v(-63.33, -117.48) * mm, "radius": 3.18 * mm});
            skCircle(sketch, "E104.4.0", {"center": v(117.7, -31.1) * mm, "radius": 3.18 * mm});
            skCircle(sketch, "E104.4.1", {"center": v(122.46, -22.85) * mm, "radius": 3.18 * mm});
            skCircle(sketch, "E104.4.2", {"center": v(127.22, -14.6) * mm, "radius": 3.18 * mm});
            skCircle(sketch, "E104.4.3", {"center": v(131.98, -6.35) * mm, "radius": 3.18 * mm});
            skCircle(sketch, "E104.4.4", {"center": v(112.93, -39.35) * mm, "radius": 3.18 * mm});
            skCircle(sketch, "E104.4.5", {"center": v(108.17, -47.6) * mm, "radius": 3.18 * mm});
            skCircle(sketch, "E104.4.6", {"center": v(103.4, -55.84) * mm, "radius": 3.18 * mm});
            skCircle(sketch, "E104.4.7", {"center": v(98.64, -64.1) * mm, "radius": 3.18 * mm});
            skCircle(sketch, "E104.4.8", {"center": v(93.88, -72.34) * mm, "radius": 3.18 * mm});
            skCircle(sketch, "E104.4.9", {"center": v(89.12, -80.6) * mm, "radius": 3.18 * mm});
            skCircle(sketch, "E104.4.10", {"center": v(84.36, -88.84) * mm, "radius": 3.18 * mm});
            skCircle(sketch, "E104.4.11", {"center": v(79.6, -97.09) * mm, "radius": 3.18 * mm});
            skCircle(sketch, "E104.4.12", {"center": v(74.83, -105.34) * mm, "radius": 3.18 * mm});
            skCircle(sketch, "E104.4.13", {"center": v(70.07, -113.59) * mm, "radius": 3.18 * mm});
            skCircle(sketch, "E104.5.0", {"center": v(85.78, 86.38) * mm, "radius": 3.18 * mm});
            skCircle(sketch, "E104.5.1", {"center": v(81.02, 94.63) * mm, "radius": 3.18 * mm});
            skCircle(sketch, "E104.5.2", {"center": v(76.25, 102.88) * mm, "radius": 3.18 * mm});
            skCircle(sketch, "E104.5.3", {"center": v(71.5, 111.13) * mm, "radius": 3.18 * mm});
            skCircle(sketch, "E104.5.4", {"center": v(90.54, 78.13) * mm, "radius": 3.18 * mm});
            skCircle(sketch, "E104.5.5", {"center": v(95.3, 69.88) * mm, "radius": 3.18 * mm});
            skCircle(sketch, "E104.5.6", {"center": v(100.07, 61.63) * mm, "radius": 3.18 * mm});
            skCircle(sketch, "E104.5.7", {"center": v(104.83, 53.38) * mm, "radius": 3.18 * mm});
            skCircle(sketch, "E104.5.8", {"center": v(109.6, 45.13) * mm, "radius": 3.18 * mm});
            skCircle(sketch, "E104.5.9", {"center": v(114.35, 36.88) * mm, "radius": 3.18 * mm});
            skCircle(sketch, "E104.5.10", {"center": v(119.12, 28.64) * mm, "radius": 3.18 * mm});
            skCircle(sketch, "E104.5.11", {"center": v(123.88, 20.39) * mm, "radius": 3.18 * mm});
            skCircle(sketch, "E104.5.12", {"center": v(128.64, 12.14) * mm, "radius": 3.18 * mm});
            skCircle(sketch, "E104.5.13", {"center": v(133.4, 3.89) * mm, "radius": 3.18 * mm});
            skLineSegment(sketch, "E105", {"start": v(-90.74, 10.16) * mm, "end": v(90.74, 10.16) * mm, "construction": true});
            skCircle(sketch, "E106", {"center": v(-90.74, 10.16) * mm, "radius": 3.18 * mm});
            skCircle(sketch, "E107.1.0.0", {"center": v(-81.21, 10.16) * mm, "radius": 3.18 * mm});
            skCircle(sketch, "E107.2.0.0", {"center": v(-71.69, 10.16) * mm, "radius": 3.18 * mm});
            skCircle(sketch, "E107.3.0.0", {"center": v(-62.16, 10.16) * mm, "radius": 3.18 * mm});
            skCircle(sketch, "E107.4.0.0", {"center": v(-52.64, 10.16) * mm, "radius": 3.18 * mm});
            skCircle(sketch, "E107.5.0.0", {"center": v(-43.11, 10.16) * mm, "radius": 3.18 * mm});
            skCircle(sketch, "E107.6.0.0", {"center": v(-33.59, 10.16) * mm, "radius": 3.18 * mm});
            skCircle(sketch, "E107.7.0.0", {"center": v(-24.06, 10.16) * mm, "radius": 3.18 * mm});
            skCircle(sketch, "E107.8.0.0", {"center": v(-14.54, 10.16) * mm, "radius": 3.18 * mm});
            skCircle(sketch, "E107.9.0.0", {"center": v(-5.01, 10.16) * mm, "radius": 3.18 * mm});
            skCircle(sketch, "E107.10.0.0", {"center": v(4.51, 10.16) * mm, "radius": 3.18 * mm});
            skCircle(sketch, "E107.11.0.0", {"center": v(14.04, 10.16) * mm, "radius": 3.18 * mm});
            skCircle(sketch, "E107.12.0.0", {"center": v(23.56, 10.16) * mm, "radius": 3.18 * mm});
            skCircle(sketch, "E107.13.0.0", {"center": v(33.09, 10.16) * mm, "radius": 3.18 * mm});
            skCircle(sketch, "E107.14.0.0", {"center": v(42.61, 10.16) * mm, "radius": 3.18 * mm});
            skCircle(sketch, "E107.15.0.0", {"center": v(52.14, 10.16) * mm, "radius": 3.18 * mm});
            skCircle(sketch, "E107.16.0.0", {"center": v(61.66, 10.16) * mm, "radius": 3.18 * mm});
            skCircle(sketch, "E107.17.0.0", {"center": v(71.19, 10.16) * mm, "radius": 3.18 * mm});
            skCircle(sketch, "E107.18.0.0", {"center": v(80.71, 10.16) * mm, "radius": 3.18 * mm});
            skCircle(sketch, "E107.19.0.0", {"center": v(90.24, 10.16) * mm, "radius": 3.18 * mm});
            skLineSegment(sketch, "E107.direction1", {"start": v(-90.74, 10.16) * mm, "end": v(-81.21, 10.16) * mm, "construction": true});
            skCircle(sketch, "E108", {"center": v(-106.78, -15.88) * mm, "radius": 7.94 * mm});
            skCircle(sketch, "E109", {"center": v(-106.78, 15.88) * mm, "radius": 9.53 * mm});
            skCircle(sketch, "E110", {"center": v(106.78, 15.88) * mm, "radius": 9.53 * mm});
            skCircle(sketch, "E111", {"center": v(106.78, -15.87) * mm, "radius": 7.94 * mm});
            skPoint(sketch, "E112", {"position": v(-120.98, 0) * mm});
            skSolve(sketch);
        }
        {
            var Q0;
            Q0 = qSketchRegion(id + "F6", true);
            var Q1;
            {var subQ0=sQuery(id+"F1.wireOp",EDGE,"E24");var subQ1=sQuery(id+"F1.wireOp",EDGE,"E23");var subQ2=sQuery(id+"F1.wireOp",EDGE,"E22");var subQ3=sQuery(id+"F1.wireOp",EDGE,"E21");var subQ4=sQuery(id+"F1.wireOp",EDGE,"E20");var subQ5=sQuery(id+"F1.wireOp",EDGE,"E19");Q1=makeQuery(id+"F3.boolean.opBoolean","MERGE",FACE,{"derivedFrom":[makeQuery(id+"F2.opExtrude","CAP_FACE",FACE,{"disambiguationData":[OSD([sQuery(id+"F1.wireOp",EDGE,"E10"),sQuery(id+"F1.wireOp",EDGE,"E11"),sQuery(id+"F1.wireOp",EDGE,"E12"),sQuery(id+"F1.wireOp",EDGE,"E13"),sQuery(id+"F1.wireOp",EDGE,"E14"),sQuery(id+"F1.wireOp",EDGE,"E15"),sQuery(id+"F1.wireOp",EDGE,"E16"),sQuery(id+"F1.wireOp",EDGE,"E17"),sQuery(id+"F1.wireOp",EDGE,"E18.1"),sQuery(id+"F1.wireOp",EDGE,"E18.2"),sQuery(id+"F1.wireOp",EDGE,"E18.4"),sQuery(id+"F1.wireOp",EDGE,"E18.5"),subQ5,subQ4,subQ3,subQ2,subQ1,subQ0,sQuery(id+"F1.wireOp",EDGE,"E27"),sQuery(id+"F1.wireOp",EDGE,"E28.filletArc"),sQuery(id+"F1.wireOp",EDGE,"E29.filletArc"),sQuery(id+"F1.wireOp",EDGE,"E34"),sQuery(id+"F1.wireOp",EDGE,"E37"),sQuery(id+"F1.wireOp",EDGE,"E38"),sQuery(id+"F1.wireOp",EDGE,"E39"),sQuery(id+"F1.wireOp",EDGE,"E42"),sQuery(id+"F1.wireOp",EDGE,"E47.filletArc"),sQuery(id+"F1.wireOp",EDGE,"E48.filletArc"),sQuery(id+"F1.wireOp",EDGE,"E49.filletArc"),sQuery(id+"F1.wireOp",EDGE,"E50.filletArc"),sQuery(id+"F1.wireOp",EDGE,"E51.filletArc"),sQuery(id+"F1.wireOp",EDGE,"E52.filletArc"),sQuery(id+"F1.wireOp",EDGE,"E53.filletArc"),sQuery(id+"F1.wireOp",EDGE,"E54.filletArc"),sQuery(id+"F1.wireOp",EDGE,"E55"),sQuery(id+"F1.wireOp",EDGE,"E56"),sQuery(id+"F1.wireOp",EDGE,"E58.filletArc"),sQuery(id+"F1.wireOp",EDGE,"E60"),sQuery(id+"F1.wireOp",EDGE,"E61"),sQuery(id+"F1.wireOp",EDGE,"E63.filletArc"),sQuery(id+"F1.wireOp",EDGE,"E66.MirrorCS"),sQuery(id+"F1.wireOp",EDGE,"E67.MirrorCS"),sQuery(id+"F1.wireOp",EDGE,"E68.MirrorCS"),sQuery(id+"F1.wireOp",EDGE,"E69.MirrorCS"),sQuery(id+"F1.wireOp",EDGE,"E70.MirrorCS"),sQuery(id+"F1.wireOp",EDGE,"E71.MirrorCS"),sQuery(id+"F1.wireOp",EDGE,"E80"),sQuery(id+"F1.wireOp",EDGE,"E81"),sQuery(id+"F1.wireOp",EDGE,"E82"),sQuery(id+"F1.wireOp",EDGE,"E83"),sQuery(id+"F1.wireOp",EDGE,"E84"),sQuery(id+"F1.wireOp",EDGE,"E85"),sQuery(id+"F1.wireOp",EDGE,"E86"),sQuery(id+"F1.wireOp",EDGE,"E87"),sQuery(id+"F1.wireOp",EDGE,"E88"),sQuery(id+"F1.wireOp",EDGE,"E89"),sQuery(id+"F1.wireOp",EDGE,"E92"),sQuery(id+"F1.wireOp",EDGE,"E93")])],"isStart":true}),makeQuery(id+"F3.opExtrude","CAP_FACE",FACE,{"disambiguationData":[OSD([subQ5])],"isStart":true}),makeQuery(id+"F3.opExtrude","CAP_FACE",FACE,{"disambiguationData":[OSD([subQ4])],"isStart":true}),makeQuery(id+"F3.opExtrude","CAP_FACE",FACE,{"disambiguationData":[OSD([subQ3])],"isStart":true}),makeQuery(id+"F3.opExtrude","CAP_FACE",FACE,{"disambiguationData":[OSD([subQ2])],"isStart":true}),makeQuery(id+"F3.opExtrude","CAP_FACE",FACE,{"disambiguationData":[OSD([subQ1])],"isStart":true}),makeQuery(id+"F3.opExtrude","CAP_FACE",FACE,{"disambiguationData":[OSD([subQ0])],"isStart":true})]});}
            extrude(context, id + "F7", {"entities" : qUnion([Q0]), "operationType" : NewBodyOperationType.REMOVE, "endBound" : BoundingType.UP_TO_SURFACE, "oppositeDirection" : true, "endBoundEntityFace" : qUnion([Q1]), "depth" : 25.4 * mm});
        }
        {
            var Q0;
            Q0=makeQuery(id+"F2.opExtrude","CAP_FACE",FACE,{"disambiguationData":[OSD([sQuery(id+"F1.wireOp",EDGE,"E10"),sQuery(id+"F1.wireOp",EDGE,"E11"),sQuery(id+"F1.wireOp",EDGE,"E12"),sQuery(id+"F1.wireOp",EDGE,"E13"),sQuery(id+"F1.wireOp",EDGE,"E14"),sQuery(id+"F1.wireOp",EDGE,"E15"),sQuery(id+"F1.wireOp",EDGE,"E16"),sQuery(id+"F1.wireOp",EDGE,"E17"),sQuery(id+"F1.wireOp",EDGE,"E18.1"),sQuery(id+"F1.wireOp",EDGE,"E18.2"),sQuery(id+"F1.wireOp",EDGE,"E18.4"),sQuery(id+"F1.wireOp",EDGE,"E18.5"),sQuery(id+"F1.wireOp",EDGE,"E19"),sQuery(id+"F1.wireOp",EDGE,"E20"),sQuery(id+"F1.wireOp",EDGE,"E21"),sQuery(id+"F1.wireOp",EDGE,"E22"),sQuery(id+"F1.wireOp",EDGE,"E23"),sQuery(id+"F1.wireOp",EDGE,"E24"),sQuery(id+"F1.wireOp",EDGE,"E27"),sQuery(id+"F1.wireOp",EDGE,"E28.filletArc"),sQuery(id+"F1.wireOp",EDGE,"E29.filletArc"),sQuery(id+"F1.wireOp",EDGE,"E34"),sQuery(id+"F1.wireOp",EDGE,"E37"),sQuery(id+"F1.wireOp",EDGE,"E38"),sQuery(id+"F1.wireOp",EDGE,"E39"),sQuery(id+"F1.wireOp",EDGE,"E42"),sQuery(id+"F1.wireOp",EDGE,"E47.filletArc"),sQuery(id+"F1.wireOp",EDGE,"E48.filletArc"),sQuery(id+"F1.wireOp",EDGE,"E49.filletArc"),sQuery(id+"F1.wireOp",EDGE,"E50.filletArc"),sQuery(id+"F1.wireOp",EDGE,"E51.filletArc"),sQuery(id+"F1.wireOp",EDGE,"E52.filletArc"),sQuery(id+"F1.wireOp",EDGE,"E53.filletArc"),sQuery(id+"F1.wireOp",EDGE,"E54.filletArc"),sQuery(id+"F1.wireOp",EDGE,"E55"),sQuery(id+"F1.wireOp",EDGE,"E56"),sQuery(id+"F1.wireOp",EDGE,"E58.filletArc"),sQuery(id+"F1.wireOp",EDGE,"E60"),sQuery(id+"F1.wireOp",EDGE,"E61"),sQuery(id+"F1.wireOp",EDGE,"E63.filletArc"),sQuery(id+"F1.wireOp",EDGE,"E66.MirrorCS"),sQuery(id+"F1.wireOp",EDGE,"E67.MirrorCS"),sQuery(id+"F1.wireOp",EDGE,"E68.MirrorCS"),sQuery(id+"F1.wireOp",EDGE,"E69.MirrorCS"),sQuery(id+"F1.wireOp",EDGE,"E70.MirrorCS"),sQuery(id+"F1.wireOp",EDGE,"E71.MirrorCS"),sQuery(id+"F1.wireOp",EDGE,"E80"),sQuery(id+"F1.wireOp",EDGE,"E81"),sQuery(id+"F1.wireOp",EDGE,"E82"),sQuery(id+"F1.wireOp",EDGE,"E83"),sQuery(id+"F1.wireOp",EDGE,"E84"),sQuery(id+"F1.wireOp",EDGE,"E85"),sQuery(id+"F1.wireOp",EDGE,"E86"),sQuery(id+"F1.wireOp",EDGE,"E87"),sQuery(id+"F1.wireOp",EDGE,"E88"),sQuery(id+"F1.wireOp",EDGE,"E89"),sQuery(id+"F1.wireOp",EDGE,"E92"),sQuery(id+"F1.wireOp",EDGE,"E93")])],"isStart":false});
            var sketch = newSketch(context, id + "F8", { "sketchPlane" : qUnion([Q0])});
            skCircle(sketch, "E113", {"center": v(0, 0) * mm, "radius": 101.6 * mm});
            skSolve(sketch);
        }
        {
            var Q0;
            {var subQ5=makeQuery(id+"F2.opExtrude","CAP_EDGE",EDGE,{"disambiguationData":[OSD([sQuery(id+"F1.wireOp",EDGE,"E58.filletArc")])],"isStart":false});Q0=makeQuery(id+"F8.imprint","IMPRINT",FACE,{"disambiguationData":[TD([[makeQuery(id+"F8.imprint","IMPRINT",EDGE,{"derivedFrom":subQ5}),1.0]])]});}
            var Q1;
            {var subQ5=makeQuery(id+"F2.opExtrude","CAP_EDGE",EDGE,{"disambiguationData":[OSD([sQuery(id+"F1.wireOp",EDGE,"E63.filletArc")])],"isStart":false});Q1=makeQuery(id+"F8.imprint","IMPRINT",FACE,{"disambiguationData":[TD([[makeQuery(id+"F8.imprint","IMPRINT",EDGE,{"derivedFrom":subQ5}),1.0]])]});}
            var Q2;
            {var subQ5=makeQuery(id+"F2.opExtrude","CAP_EDGE",EDGE,{"disambiguationData":[OSD([sQuery(id+"F1.wireOp",EDGE,"E69.MirrorCS")])],"isStart":false});Q2=makeQuery(id+"F8.imprint","IMPRINT",FACE,{"disambiguationData":[TD([[makeQuery(id+"F8.imprint","IMPRINT",EDGE,{"derivedFrom":subQ5}),-1.0]])]});}
            var Q3;
            {var subQ5=makeQuery(id+"F2.opExtrude","CAP_EDGE",EDGE,{"disambiguationData":[OSD([sQuery(id+"F1.wireOp",EDGE,"E67.MirrorCS")])],"isStart":false});Q3=makeQuery(id+"F8.imprint","IMPRINT",FACE,{"disambiguationData":[TD([[makeQuery(id+"F8.imprint","IMPRINT",EDGE,{"derivedFrom":subQ5}),-1.0]])]});}
            var Q4;
            {var subQ0=sQuery(id+"F1.wireOp",EDGE,"E24");var subQ1=sQuery(id+"F1.wireOp",EDGE,"E23");var subQ2=sQuery(id+"F1.wireOp",EDGE,"E22");var subQ3=sQuery(id+"F1.wireOp",EDGE,"E21");var subQ4=sQuery(id+"F1.wireOp",EDGE,"E20");var subQ5=sQuery(id+"F1.wireOp",EDGE,"E19");Q4=makeQuery(id+"F3.boolean.opBoolean","MERGE",FACE,{"derivedFrom":[makeQuery(id+"F2.opExtrude","CAP_FACE",FACE,{"disambiguationData":[OSD([sQuery(id+"F1.wireOp",EDGE,"E10"),sQuery(id+"F1.wireOp",EDGE,"E11"),sQuery(id+"F1.wireOp",EDGE,"E12"),sQuery(id+"F1.wireOp",EDGE,"E13"),sQuery(id+"F1.wireOp",EDGE,"E14"),sQuery(id+"F1.wireOp",EDGE,"E15"),sQuery(id+"F1.wireOp",EDGE,"E16"),sQuery(id+"F1.wireOp",EDGE,"E17"),sQuery(id+"F1.wireOp",EDGE,"E18.1"),sQuery(id+"F1.wireOp",EDGE,"E18.2"),sQuery(id+"F1.wireOp",EDGE,"E18.4"),sQuery(id+"F1.wireOp",EDGE,"E18.5"),subQ5,subQ4,subQ3,subQ2,subQ1,subQ0,sQuery(id+"F1.wireOp",EDGE,"E27"),sQuery(id+"F1.wireOp",EDGE,"E28.filletArc"),sQuery(id+"F1.wireOp",EDGE,"E29.filletArc"),sQuery(id+"F1.wireOp",EDGE,"E34"),sQuery(id+"F1.wireOp",EDGE,"E37"),sQuery(id+"F1.wireOp",EDGE,"E38"),sQuery(id+"F1.wireOp",EDGE,"E39"),sQuery(id+"F1.wireOp",EDGE,"E42"),sQuery(id+"F1.wireOp",EDGE,"E47.filletArc"),sQuery(id+"F1.wireOp",EDGE,"E48.filletArc"),sQuery(id+"F1.wireOp",EDGE,"E49.filletArc"),sQuery(id+"F1.wireOp",EDGE,"E50.filletArc"),sQuery(id+"F1.wireOp",EDGE,"E51.filletArc"),sQuery(id+"F1.wireOp",EDGE,"E52.filletArc"),sQuery(id+"F1.wireOp",EDGE,"E53.filletArc"),sQuery(id+"F1.wireOp",EDGE,"E54.filletArc"),sQuery(id+"F1.wireOp",EDGE,"E55"),sQuery(id+"F1.wireOp",EDGE,"E56"),sQuery(id+"F1.wireOp",EDGE,"E58.filletArc"),sQuery(id+"F1.wireOp",EDGE,"E60"),sQuery(id+"F1.wireOp",EDGE,"E61"),sQuery(id+"F1.wireOp",EDGE,"E63.filletArc"),sQuery(id+"F1.wireOp",EDGE,"E66.MirrorCS"),sQuery(id+"F1.wireOp",EDGE,"E67.MirrorCS"),sQuery(id+"F1.wireOp",EDGE,"E68.MirrorCS"),sQuery(id+"F1.wireOp",EDGE,"E69.MirrorCS"),sQuery(id+"F1.wireOp",EDGE,"E70.MirrorCS"),sQuery(id+"F1.wireOp",EDGE,"E71.MirrorCS"),sQuery(id+"F1.wireOp",EDGE,"E80"),sQuery(id+"F1.wireOp",EDGE,"E81"),sQuery(id+"F1.wireOp",EDGE,"E82"),sQuery(id+"F1.wireOp",EDGE,"E83"),sQuery(id+"F1.wireOp",EDGE,"E84"),sQuery(id+"F1.wireOp",EDGE,"E85"),sQuery(id+"F1.wireOp",EDGE,"E86"),sQuery(id+"F1.wireOp",EDGE,"E87"),sQuery(id+"F1.wireOp",EDGE,"E88"),sQuery(id+"F1.wireOp",EDGE,"E89"),sQuery(id+"F1.wireOp",EDGE,"E92"),sQuery(id+"F1.wireOp",EDGE,"E93")])],"isStart":true}),makeQuery(id+"F3.opExtrude","CAP_FACE",FACE,{"disambiguationData":[OSD([subQ5])],"isStart":true}),makeQuery(id+"F3.opExtrude","CAP_FACE",FACE,{"disambiguationData":[OSD([subQ4])],"isStart":true}),makeQuery(id+"F3.opExtrude","CAP_FACE",FACE,{"disambiguationData":[OSD([subQ3])],"isStart":true}),makeQuery(id+"F3.opExtrude","CAP_FACE",FACE,{"disambiguationData":[OSD([subQ2])],"isStart":true}),makeQuery(id+"F3.opExtrude","CAP_FACE",FACE,{"disambiguationData":[OSD([subQ1])],"isStart":true}),makeQuery(id+"F3.opExtrude","CAP_FACE",FACE,{"disambiguationData":[OSD([subQ0])],"isStart":true})]});}
            extrude(context, id + "F9", {"entities" : qUnion([Q0, Q1, Q2, Q3]), "operationType" : NewBodyOperationType.REMOVE, "endBound" : BoundingType.UP_TO_SURFACE, "oppositeDirection" : true, "endBoundEntityFace" : qUnion([Q4]), "depth" : 25.4 * mm});
        }
        {
            var Q0;
            Q0=makeQuery(id+"F2.opExtrude","CAP_FACE",FACE,{"disambiguationData":[OSD([sQuery(id+"F1.wireOp",EDGE,"E10"),sQuery(id+"F1.wireOp",EDGE,"E11"),sQuery(id+"F1.wireOp",EDGE,"E12"),sQuery(id+"F1.wireOp",EDGE,"E13"),sQuery(id+"F1.wireOp",EDGE,"E14"),sQuery(id+"F1.wireOp",EDGE,"E15"),sQuery(id+"F1.wireOp",EDGE,"E16"),sQuery(id+"F1.wireOp",EDGE,"E17"),sQuery(id+"F1.wireOp",EDGE,"E18.1"),sQuery(id+"F1.wireOp",EDGE,"E18.2"),sQuery(id+"F1.wireOp",EDGE,"E18.4"),sQuery(id+"F1.wireOp",EDGE,"E18.5"),sQuery(id+"F1.wireOp",EDGE,"E19"),sQuery(id+"F1.wireOp",EDGE,"E20"),sQuery(id+"F1.wireOp",EDGE,"E21"),sQuery(id+"F1.wireOp",EDGE,"E22"),sQuery(id+"F1.wireOp",EDGE,"E23"),sQuery(id+"F1.wireOp",EDGE,"E24"),sQuery(id+"F1.wireOp",EDGE,"E27"),sQuery(id+"F1.wireOp",EDGE,"E28.filletArc"),sQuery(id+"F1.wireOp",EDGE,"E29.filletArc"),sQuery(id+"F1.wireOp",EDGE,"E34"),sQuery(id+"F1.wireOp",EDGE,"E37"),sQuery(id+"F1.wireOp",EDGE,"E38"),sQuery(id+"F1.wireOp",EDGE,"E39"),sQuery(id+"F1.wireOp",EDGE,"E42"),sQuery(id+"F1.wireOp",EDGE,"E47.filletArc"),sQuery(id+"F1.wireOp",EDGE,"E48.filletArc"),sQuery(id+"F1.wireOp",EDGE,"E49.filletArc"),sQuery(id+"F1.wireOp",EDGE,"E50.filletArc"),sQuery(id+"F1.wireOp",EDGE,"E51.filletArc"),sQuery(id+"F1.wireOp",EDGE,"E52.filletArc"),sQuery(id+"F1.wireOp",EDGE,"E53.filletArc"),sQuery(id+"F1.wireOp",EDGE,"E54.filletArc"),sQuery(id+"F1.wireOp",EDGE,"E55"),sQuery(id+"F1.wireOp",EDGE,"E56"),sQuery(id+"F1.wireOp",EDGE,"E58.filletArc"),sQuery(id+"F1.wireOp",EDGE,"E60"),sQuery(id+"F1.wireOp",EDGE,"E61"),sQuery(id+"F1.wireOp",EDGE,"E63.filletArc"),sQuery(id+"F1.wireOp",EDGE,"E66.MirrorCS"),sQuery(id+"F1.wireOp",EDGE,"E67.MirrorCS"),sQuery(id+"F1.wireOp",EDGE,"E68.MirrorCS"),sQuery(id+"F1.wireOp",EDGE,"E69.MirrorCS"),sQuery(id+"F1.wireOp",EDGE,"E70.MirrorCS"),sQuery(id+"F1.wireOp",EDGE,"E71.MirrorCS"),sQuery(id+"F1.wireOp",EDGE,"E80"),sQuery(id+"F1.wireOp",EDGE,"E81"),sQuery(id+"F1.wireOp",EDGE,"E82"),sQuery(id+"F1.wireOp",EDGE,"E83"),sQuery(id+"F1.wireOp",EDGE,"E84"),sQuery(id+"F1.wireOp",EDGE,"E85"),sQuery(id+"F1.wireOp",EDGE,"E86"),sQuery(id+"F1.wireOp",EDGE,"E87"),sQuery(id+"F1.wireOp",EDGE,"E88"),sQuery(id+"F1.wireOp",EDGE,"E89"),sQuery(id+"F1.wireOp",EDGE,"E92"),sQuery(id+"F1.wireOp",EDGE,"E93")])],"isStart":false});
            var sketch = newSketch(context, id + "F10", { "sketchPlane" : qUnion([Q0])});
            skLineSegment(sketch, "E114", {"start": v(-66.95, -93.59) * mm, "end": v(-72.03, -93.59) * mm, "construction": true});
            skLineSegment(sketch, "E115", {"start": v(-90.74, -52.39) * mm, "end": v(-95.82, -52.39) * mm, "construction": true});
            skLineSegment(sketch, "E116", {"start": v(-72.03, -93.59) * mm, "end": v(-106.96, -33.1) * mm, "construction": true});
            skCircle(sketch, "E117", {"center": v(-72.03, -93.59) * mm, "radius": 1.59 * mm});
            skCircle(sketch, "E118", {"center": v(-74.6, -89.14) * mm, "radius": 1.59 * mm});
            skCircle(sketch, "E119", {"center": v(-77.16, -84.7) * mm, "radius": 1.59 * mm});
            skCircle(sketch, "E120", {"center": v(-79.73, -80.25) * mm, "radius": 1.59 * mm});
            skCircle(sketch, "E121", {"center": v(-82.3, -75.8) * mm, "radius": 1.59 * mm});
            skCircle(sketch, "E122", {"center": v(-84.86, -71.36) * mm, "radius": 1.59 * mm});
            skCircle(sketch, "E123", {"center": v(-87.43, -66.92) * mm, "radius": 1.59 * mm});
            skCircle(sketch, "E124", {"center": v(-90, -62.47) * mm, "radius": 1.59 * mm});
            skCircle(sketch, "E125", {"center": v(-92.56, -58.03) * mm, "radius": 1.59 * mm});
            skCircle(sketch, "E126", {"center": v(-97.7, -49.14) * mm, "radius": 1.59 * mm});
            skCircle(sketch, "E127", {"center": v(-95.13, -53.58) * mm, "radius": 1.59 * mm});
            skCircle(sketch, "E128", {"center": v(-100.26, -44.7) * mm, "radius": 1.59 * mm});
            skCircle(sketch, "E129", {"center": v(-102.83, -40.25) * mm, "radius": 1.59 * mm});
            skCircle(sketch, "E130", {"center": v(-105.4, -35.8) * mm, "radius": 1.59 * mm});
            skLineSegment(sketch, "E131", {"start": v(-106.96, -33.1) * mm, "end": v(-101.19, -26.22) * mm, "construction": true});
            skCircle(sketch, "E132", {"center": v(-105.5, -31.36) * mm, "radius": 1.59 * mm});
            skSolve(sketch);
        }
        {
            var Q0;
            Q0 = qSketchRegion(id + "F10", true);
            var Q1;
            {var subQ0=sQuery(id+"F1.wireOp",EDGE,"E24");var subQ1=sQuery(id+"F1.wireOp",EDGE,"E23");var subQ2=sQuery(id+"F1.wireOp",EDGE,"E22");var subQ3=sQuery(id+"F1.wireOp",EDGE,"E21");var subQ4=sQuery(id+"F1.wireOp",EDGE,"E20");var subQ5=sQuery(id+"F1.wireOp",EDGE,"E19");Q1=makeQuery(id+"F3.boolean.opBoolean","MERGE",FACE,{"derivedFrom":[makeQuery(id+"F2.opExtrude","CAP_FACE",FACE,{"disambiguationData":[OSD([sQuery(id+"F1.wireOp",EDGE,"E10"),sQuery(id+"F1.wireOp",EDGE,"E11"),sQuery(id+"F1.wireOp",EDGE,"E12"),sQuery(id+"F1.wireOp",EDGE,"E13"),sQuery(id+"F1.wireOp",EDGE,"E14"),sQuery(id+"F1.wireOp",EDGE,"E15"),sQuery(id+"F1.wireOp",EDGE,"E16"),sQuery(id+"F1.wireOp",EDGE,"E17"),sQuery(id+"F1.wireOp",EDGE,"E18.1"),sQuery(id+"F1.wireOp",EDGE,"E18.2"),sQuery(id+"F1.wireOp",EDGE,"E18.4"),sQuery(id+"F1.wireOp",EDGE,"E18.5"),subQ5,subQ4,subQ3,subQ2,subQ1,subQ0,sQuery(id+"F1.wireOp",EDGE,"E27"),sQuery(id+"F1.wireOp",EDGE,"E28.filletArc"),sQuery(id+"F1.wireOp",EDGE,"E29.filletArc"),sQuery(id+"F1.wireOp",EDGE,"E34"),sQuery(id+"F1.wireOp",EDGE,"E37"),sQuery(id+"F1.wireOp",EDGE,"E38"),sQuery(id+"F1.wireOp",EDGE,"E39"),sQuery(id+"F1.wireOp",EDGE,"E42"),sQuery(id+"F1.wireOp",EDGE,"E47.filletArc"),sQuery(id+"F1.wireOp",EDGE,"E48.filletArc"),sQuery(id+"F1.wireOp",EDGE,"E49.filletArc"),sQuery(id+"F1.wireOp",EDGE,"E50.filletArc"),sQuery(id+"F1.wireOp",EDGE,"E51.filletArc"),sQuery(id+"F1.wireOp",EDGE,"E52.filletArc"),sQuery(id+"F1.wireOp",EDGE,"E53.filletArc"),sQuery(id+"F1.wireOp",EDGE,"E54.filletArc"),sQuery(id+"F1.wireOp",EDGE,"E55"),sQuery(id+"F1.wireOp",EDGE,"E56"),sQuery(id+"F1.wireOp",EDGE,"E58.filletArc"),sQuery(id+"F1.wireOp",EDGE,"E60"),sQuery(id+"F1.wireOp",EDGE,"E61"),sQuery(id+"F1.wireOp",EDGE,"E63.filletArc"),sQuery(id+"F1.wireOp",EDGE,"E66.MirrorCS"),sQuery(id+"F1.wireOp",EDGE,"E67.MirrorCS"),sQuery(id+"F1.wireOp",EDGE,"E68.MirrorCS"),sQuery(id+"F1.wireOp",EDGE,"E69.MirrorCS"),sQuery(id+"F1.wireOp",EDGE,"E70.MirrorCS"),sQuery(id+"F1.wireOp",EDGE,"E71.MirrorCS"),sQuery(id+"F1.wireOp",EDGE,"E80"),sQuery(id+"F1.wireOp",EDGE,"E81"),sQuery(id+"F1.wireOp",EDGE,"E82"),sQuery(id+"F1.wireOp",EDGE,"E83"),sQuery(id+"F1.wireOp",EDGE,"E84"),sQuery(id+"F1.wireOp",EDGE,"E85"),sQuery(id+"F1.wireOp",EDGE,"E86"),sQuery(id+"F1.wireOp",EDGE,"E87"),sQuery(id+"F1.wireOp",EDGE,"E88"),sQuery(id+"F1.wireOp",EDGE,"E89"),sQuery(id+"F1.wireOp",EDGE,"E92"),sQuery(id+"F1.wireOp",EDGE,"E93")])],"isStart":true}),makeQuery(id+"F3.opExtrude","CAP_FACE",FACE,{"disambiguationData":[OSD([subQ5])],"isStart":true}),makeQuery(id+"F3.opExtrude","CAP_FACE",FACE,{"disambiguationData":[OSD([subQ4])],"isStart":true}),makeQuery(id+"F3.opExtrude","CAP_FACE",FACE,{"disambiguationData":[OSD([subQ3])],"isStart":true}),makeQuery(id+"F3.opExtrude","CAP_FACE",FACE,{"disambiguationData":[OSD([subQ2])],"isStart":true}),makeQuery(id+"F3.opExtrude","CAP_FACE",FACE,{"disambiguationData":[OSD([subQ1])],"isStart":true}),makeQuery(id+"F3.opExtrude","CAP_FACE",FACE,{"disambiguationData":[OSD([subQ0])],"isStart":true})]});}
            extrude(context, id + "F11", {"entities" : qUnion([Q0]), "operationType" : NewBodyOperationType.REMOVE, "endBound" : BoundingType.UP_TO_SURFACE, "oppositeDirection" : true, "endBoundEntityFace" : qUnion([Q1]), "depth" : 25.4 * mm});
        }
        {
            var Q0;
            Q0=makeQuery(id+"F2.opExtrude","CAP_FACE",FACE,{"disambiguationData":[OSD([sQuery(id+"F1.wireOp",EDGE,"E10"),sQuery(id+"F1.wireOp",EDGE,"E11"),sQuery(id+"F1.wireOp",EDGE,"E12"),sQuery(id+"F1.wireOp",EDGE,"E13"),sQuery(id+"F1.wireOp",EDGE,"E14"),sQuery(id+"F1.wireOp",EDGE,"E15"),sQuery(id+"F1.wireOp",EDGE,"E16"),sQuery(id+"F1.wireOp",EDGE,"E17"),sQuery(id+"F1.wireOp",EDGE,"E18.1"),sQuery(id+"F1.wireOp",EDGE,"E18.2"),sQuery(id+"F1.wireOp",EDGE,"E18.4"),sQuery(id+"F1.wireOp",EDGE,"E18.5"),sQuery(id+"F1.wireOp",EDGE,"E19"),sQuery(id+"F1.wireOp",EDGE,"E20"),sQuery(id+"F1.wireOp",EDGE,"E21"),sQuery(id+"F1.wireOp",EDGE,"E22"),sQuery(id+"F1.wireOp",EDGE,"E23"),sQuery(id+"F1.wireOp",EDGE,"E24"),sQuery(id+"F1.wireOp",EDGE,"E27"),sQuery(id+"F1.wireOp",EDGE,"E28.filletArc"),sQuery(id+"F1.wireOp",EDGE,"E29.filletArc"),sQuery(id+"F1.wireOp",EDGE,"E34"),sQuery(id+"F1.wireOp",EDGE,"E37"),sQuery(id+"F1.wireOp",EDGE,"E38"),sQuery(id+"F1.wireOp",EDGE,"E39"),sQuery(id+"F1.wireOp",EDGE,"E42"),sQuery(id+"F1.wireOp",EDGE,"E47.filletArc"),sQuery(id+"F1.wireOp",EDGE,"E48.filletArc"),sQuery(id+"F1.wireOp",EDGE,"E49.filletArc"),sQuery(id+"F1.wireOp",EDGE,"E50.filletArc"),sQuery(id+"F1.wireOp",EDGE,"E51.filletArc"),sQuery(id+"F1.wireOp",EDGE,"E52.filletArc"),sQuery(id+"F1.wireOp",EDGE,"E53.filletArc"),sQuery(id+"F1.wireOp",EDGE,"E54.filletArc"),sQuery(id+"F1.wireOp",EDGE,"E55"),sQuery(id+"F1.wireOp",EDGE,"E56"),sQuery(id+"F1.wireOp",EDGE,"E58.filletArc"),sQuery(id+"F1.wireOp",EDGE,"E60"),sQuery(id+"F1.wireOp",EDGE,"E61"),sQuery(id+"F1.wireOp",EDGE,"E63.filletArc"),sQuery(id+"F1.wireOp",EDGE,"E66.MirrorCS"),sQuery(id+"F1.wireOp",EDGE,"E67.MirrorCS"),sQuery(id+"F1.wireOp",EDGE,"E68.MirrorCS"),sQuery(id+"F1.wireOp",EDGE,"E69.MirrorCS"),sQuery(id+"F1.wireOp",EDGE,"E70.MirrorCS"),sQuery(id+"F1.wireOp",EDGE,"E71.MirrorCS"),sQuery(id+"F1.wireOp",EDGE,"E80"),sQuery(id+"F1.wireOp",EDGE,"E81"),sQuery(id+"F1.wireOp",EDGE,"E82"),sQuery(id+"F1.wireOp",EDGE,"E83"),sQuery(id+"F1.wireOp",EDGE,"E84"),sQuery(id+"F1.wireOp",EDGE,"E85"),sQuery(id+"F1.wireOp",EDGE,"E86"),sQuery(id+"F1.wireOp",EDGE,"E87"),sQuery(id+"F1.wireOp",EDGE,"E88"),sQuery(id+"F1.wireOp",EDGE,"E89"),sQuery(id+"F1.wireOp",EDGE,"E92"),sQuery(id+"F1.wireOp",EDGE,"E93")])],"isStart":false});
            var sketch = newSketch(context, id + "F12", { "sketchPlane" : qUnion([Q0])});
            skCircle(sketch, "E133", {"center": v(-93.8, -2.47) * mm, "radius": 4.76 * mm});
            skCircle(sketch, "E134", {"center": v(94.13, -2.47) * mm, "radius": 4.76 * mm});
            skSolve(sketch);
        }
        {
            var Q0;
            Q0 = qSketchRegion(id + "F12", true);
            var Q1;
            {var subQ0=sQuery(id+"F1.wireOp",EDGE,"E24");var subQ1=sQuery(id+"F1.wireOp",EDGE,"E23");var subQ2=sQuery(id+"F1.wireOp",EDGE,"E22");var subQ3=sQuery(id+"F1.wireOp",EDGE,"E21");var subQ4=sQuery(id+"F1.wireOp",EDGE,"E20");var subQ5=sQuery(id+"F1.wireOp",EDGE,"E19");Q1=makeQuery(id+"F3.boolean.opBoolean","MERGE",FACE,{"derivedFrom":[makeQuery(id+"F2.opExtrude","CAP_FACE",FACE,{"disambiguationData":[OSD([sQuery(id+"F1.wireOp",EDGE,"E10"),sQuery(id+"F1.wireOp",EDGE,"E11"),sQuery(id+"F1.wireOp",EDGE,"E12"),sQuery(id+"F1.wireOp",EDGE,"E13"),sQuery(id+"F1.wireOp",EDGE,"E14"),sQuery(id+"F1.wireOp",EDGE,"E15"),sQuery(id+"F1.wireOp",EDGE,"E16"),sQuery(id+"F1.wireOp",EDGE,"E17"),sQuery(id+"F1.wireOp",EDGE,"E18.1"),sQuery(id+"F1.wireOp",EDGE,"E18.2"),sQuery(id+"F1.wireOp",EDGE,"E18.4"),sQuery(id+"F1.wireOp",EDGE,"E18.5"),subQ5,subQ4,subQ3,subQ2,subQ1,subQ0,sQuery(id+"F1.wireOp",EDGE,"E27"),sQuery(id+"F1.wireOp",EDGE,"E28.filletArc"),sQuery(id+"F1.wireOp",EDGE,"E29.filletArc"),sQuery(id+"F1.wireOp",EDGE,"E34"),sQuery(id+"F1.wireOp",EDGE,"E37"),sQuery(id+"F1.wireOp",EDGE,"E38"),sQuery(id+"F1.wireOp",EDGE,"E39"),sQuery(id+"F1.wireOp",EDGE,"E42"),sQuery(id+"F1.wireOp",EDGE,"E47.filletArc"),sQuery(id+"F1.wireOp",EDGE,"E48.filletArc"),sQuery(id+"F1.wireOp",EDGE,"E49.filletArc"),sQuery(id+"F1.wireOp",EDGE,"E50.filletArc"),sQuery(id+"F1.wireOp",EDGE,"E51.filletArc"),sQuery(id+"F1.wireOp",EDGE,"E52.filletArc"),sQuery(id+"F1.wireOp",EDGE,"E53.filletArc"),sQuery(id+"F1.wireOp",EDGE,"E54.filletArc"),sQuery(id+"F1.wireOp",EDGE,"E55"),sQuery(id+"F1.wireOp",EDGE,"E56"),sQuery(id+"F1.wireOp",EDGE,"E58.filletArc"),sQuery(id+"F1.wireOp",EDGE,"E60"),sQuery(id+"F1.wireOp",EDGE,"E61"),sQuery(id+"F1.wireOp",EDGE,"E63.filletArc"),sQuery(id+"F1.wireOp",EDGE,"E66.MirrorCS"),sQuery(id+"F1.wireOp",EDGE,"E67.MirrorCS"),sQuery(id+"F1.wireOp",EDGE,"E68.MirrorCS"),sQuery(id+"F1.wireOp",EDGE,"E69.MirrorCS"),sQuery(id+"F1.wireOp",EDGE,"E70.MirrorCS"),sQuery(id+"F1.wireOp",EDGE,"E71.MirrorCS"),sQuery(id+"F1.wireOp",EDGE,"E80"),sQuery(id+"F1.wireOp",EDGE,"E81"),sQuery(id+"F1.wireOp",EDGE,"E82"),sQuery(id+"F1.wireOp",EDGE,"E83"),sQuery(id+"F1.wireOp",EDGE,"E84"),sQuery(id+"F1.wireOp",EDGE,"E85"),sQuery(id+"F1.wireOp",EDGE,"E86"),sQuery(id+"F1.wireOp",EDGE,"E87"),sQuery(id+"F1.wireOp",EDGE,"E88"),sQuery(id+"F1.wireOp",EDGE,"E89"),sQuery(id+"F1.wireOp",EDGE,"E92"),sQuery(id+"F1.wireOp",EDGE,"E93")])],"isStart":true}),makeQuery(id+"F3.opExtrude","CAP_FACE",FACE,{"disambiguationData":[OSD([subQ5])],"isStart":true}),makeQuery(id+"F3.opExtrude","CAP_FACE",FACE,{"disambiguationData":[OSD([subQ4])],"isStart":true}),makeQuery(id+"F3.opExtrude","CAP_FACE",FACE,{"disambiguationData":[OSD([subQ3])],"isStart":true}),makeQuery(id+"F3.opExtrude","CAP_FACE",FACE,{"disambiguationData":[OSD([subQ2])],"isStart":true}),makeQuery(id+"F3.opExtrude","CAP_FACE",FACE,{"disambiguationData":[OSD([subQ1])],"isStart":true}),makeQuery(id+"F3.opExtrude","CAP_FACE",FACE,{"disambiguationData":[OSD([subQ0])],"isStart":true})]});}
            extrude(context, id + "F13", {"entities" : qUnion([Q0]), "operationType" : NewBodyOperationType.REMOVE, "endBound" : BoundingType.UP_TO_SURFACE, "oppositeDirection" : true, "endBoundEntityFace" : qUnion([Q1]), "depth" : 25.4 * mm});
        }
    });
